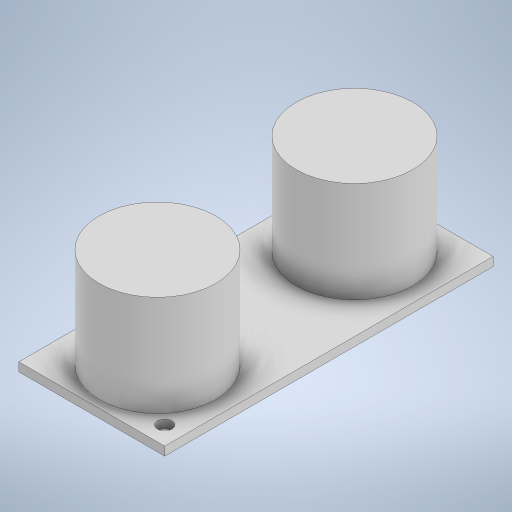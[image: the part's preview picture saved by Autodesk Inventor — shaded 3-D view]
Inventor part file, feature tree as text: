
AUTODESK INVENTOR PART (.ipt)
format: ipt  version: 2024 (Build 280153000, 153)  size: 254,976 bytes
history: native  units: mm
features: extrude x2, sketch x2, other x1
ambient origin geometry x8: Origin, YZ Plane, XZ Plane, XY Plane, X Axis, Y Axis, Z Axis, Center Point
bodies: Body1 (feature_tree)
feature tree (5):
  other  "솔리드1"
  extrude  "돌출1"  Depth=20.0mm
  extrude  "돌출2"  Depth=45.0mm
  sketch  "스케치1"
  sketch  "스케치2"
